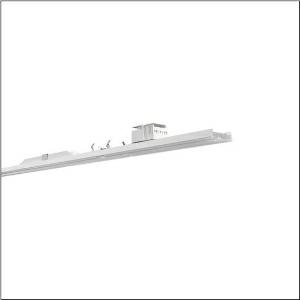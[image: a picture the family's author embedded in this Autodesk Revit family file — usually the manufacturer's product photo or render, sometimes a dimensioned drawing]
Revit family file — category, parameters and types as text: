
# Revit family: licross_r__21_recessed_mo_52tl14dnd7xf_36eb
name_source: partatom
category: Lighting Fixtures
units: mm (PartAtom-declared; Revit-internal decimal feet)

## family parameters
Cut with Voids When Loaded = No
Host = Face
Light Source = No
Part Type = Normal
Room Calculation Point = No
Round Connector Dimension = Use Diameter
Shared = No

## types (1)
- --- (1 x LED, 7330 lm, 61.1 W, 4000K)
    Apparent Load = 61 VA
    CIE Flux Codes = 56 84 97 100 100
    Color Rendering = 90
    Color Temperature = 4000K
    Default Elevation = 1800 mm
    Description = Licross® 21 Recessed MO, luminaire insert, of sheet steel, galvanised, coil coated, white, length: 1.500mm, width: 66mm, height: 67mm, LED rated luminous flux: 7.330lm, light colour: 940, control gear: DALI 2, control gear: ECG DALI, with plug, 5-pole, with phase selection, mains connection: 220..240V, AC, 50/60Hz, halogen-free wiring, primary optical cover: cover, of PMMA, light emission: direct distribution, primary light characteristic: asymmetric, protection rating (complete): IP40, insulation class (complete): insulation class I (protective earthing), certification: CE, ENEC, VDE, UKCA, protection symbol: D if used in an environment without relevant dust loads with corresponding accessories, permissible ambient temperature for indoor applications: -25..+35°C, corresponds to IFS (International Featured Standards) requirements for safety and quality in the food industry, reducing of maximum allowable ambient temperature of 5°C with ceiling mounting, packaging unit: 1 piece
    Height = 58 mm
    Lamp = 1 x LED
    Lamp Light Flux = 7330 lm
    Lamp Power = 61.1 W
    Lamp count = 1
    Length = 1500 mm
    Luminous efficacy = 120 lm/W
    Manufacturer = Siteco
    ModVariant = No
    Model = 52TL14DND7XF
    Mounting Place = Ceiling
    Mounting Type = Pendant
    Number of Poles = 1
    OnlyDefault = Yes
    Power Factor = 1
    Product Name = Licross® 21 Recessed MO
    Product group = luminaire insert
    ProductGroupID = 902
    Protection Class = Protection class I
    Protection Degree = IP 40
    RLX_Detail_Level = 1
    RlxData = <blob elided: 22921 chars, md5=0c0657a9>
    Socket = socket
    Standby Power = 0 W
    System Light Flux = 7330 lm
    System Power = 61 W
    Type Comments = factory setting: luminous flux: 100 % | dim-lin: 254 | 405 mA
    Type Image = l_1266722.jpg
    URL = http://relux.com
    VarID = @adj_129239
    Voltage = 0 V
    Weight = 0.00 kg
    Width = 66 mm

## geometry (parser evidence)
native form markers: Blend x4, Sweep x10
no freeform markers — native parametric forms only
